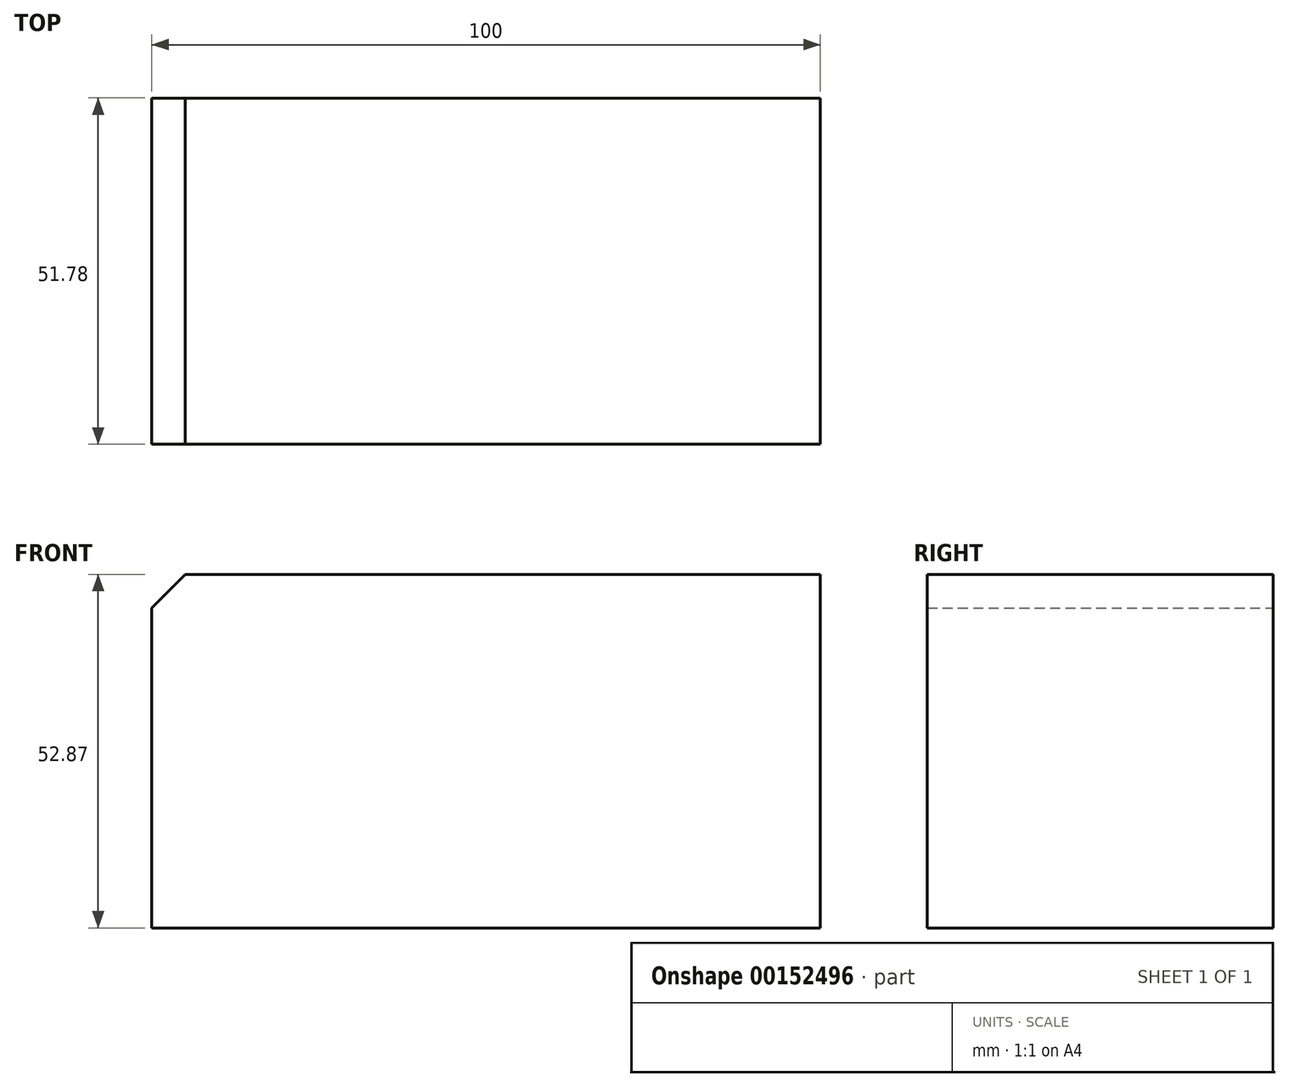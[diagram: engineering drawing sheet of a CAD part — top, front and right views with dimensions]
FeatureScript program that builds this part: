
annotation { "Feature Type Name" : "Feature", "Feature Type Description" : "" }
export const myFeature = defineFeature(function(context is Context, id is Id, definition is map)
    precondition{}
    {
        {
            var Q0;
            Q0=qCreatedBy(makeId("Right.planeOp"),FACE);
            var sketch = newSketch(context, id + "F0", { "sketchPlane" : qUnion([Q0])});
            skLineSegment(sketch, "E0.bottom", {"start": v(0, 0) * mm, "end": v(51.78, 0) * mm});
            skLineSegment(sketch, "E0.top", {"start": v(0, -52.87) * mm, "end": v(51.78, -52.87) * mm});
            skLineSegment(sketch, "E0.left", {"start": v(0, 0) * mm, "end": v(0, -52.87) * mm});
            skLineSegment(sketch, "E0.right", {"start": v(51.78, 0) * mm, "end": v(51.78, -52.87) * mm});
            skSolve(sketch);
        }
        {
            var Q0;
            Q0=makeQuery(id+"F0.imprint","IMPRINT",FACE,{"disambiguationData":[TD([[makeQuery(id+"F0.imprint","IMPRINT",EDGE,{"derivedFrom":sQuery(id+"F0.wireOp",EDGE,"E0.bottom")}),-1.0]])]});
            extrude(context, id + "F1", {"entities" : qUnion([Q0]), "depth" : 100 * mm});
        }
        {
            var Q0;
            Q0=makeQuery(id+"F1.opExtrude","CAP_EDGE",EDGE,{"disambiguationData":[OSD([sQuery(id+"F0.wireOp",EDGE,"E0.bottom")])],"isStart":true});
            chamfer(context, id + "F2", {"entities" : qUnion([Q0]), "width" : 5 * mm, "tangentPropagation" : true});
        }
    });
